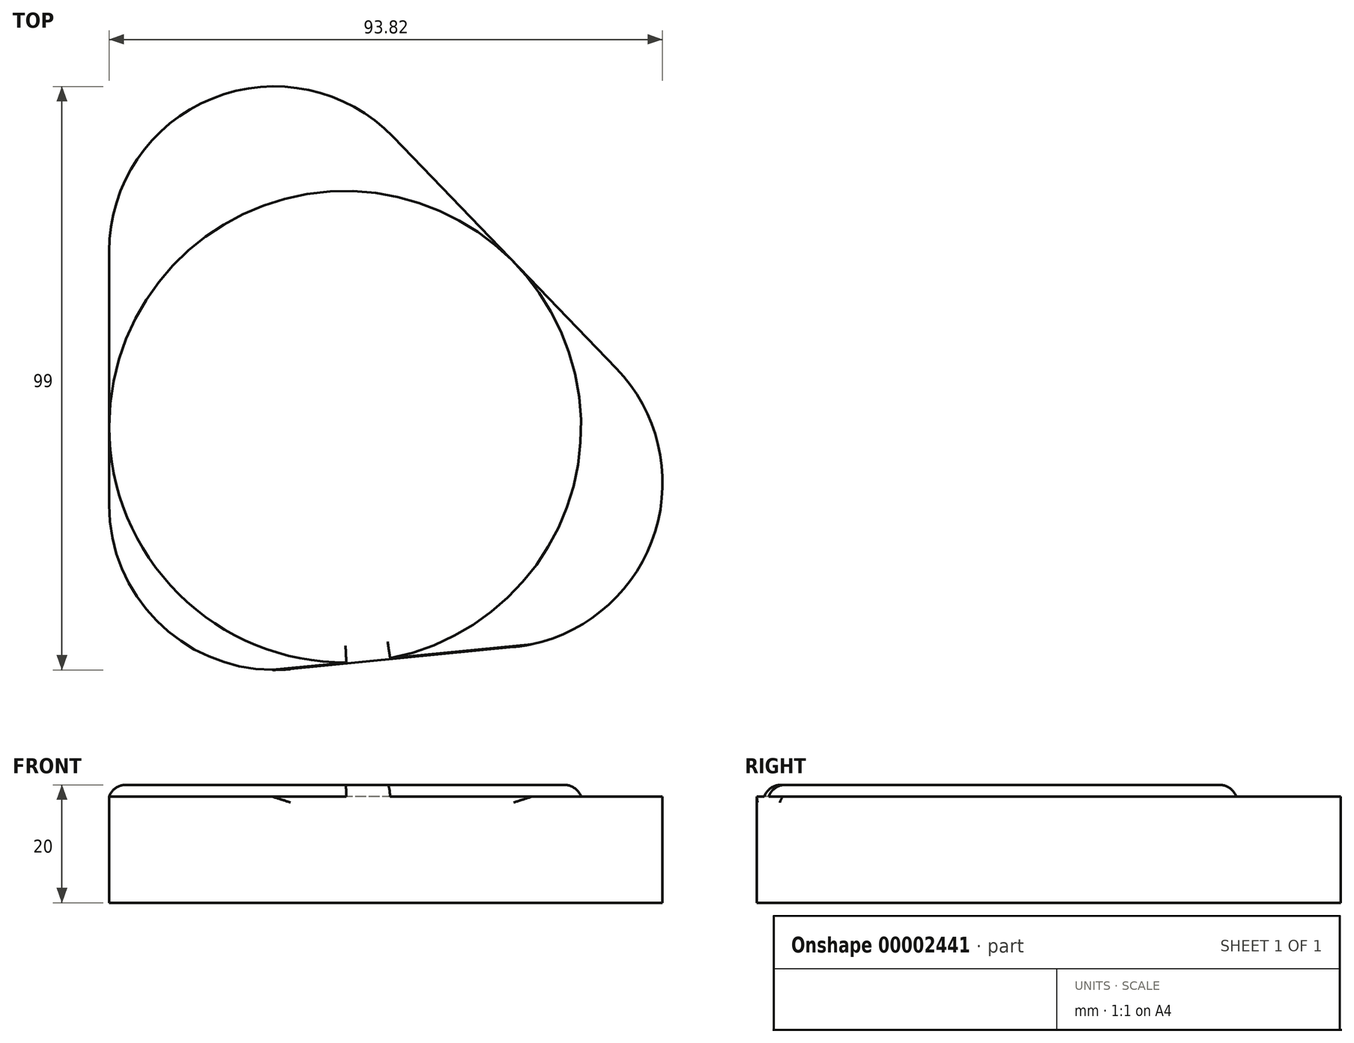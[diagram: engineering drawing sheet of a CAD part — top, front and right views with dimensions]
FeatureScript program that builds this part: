
annotation { "Feature Type Name" : "Feature", "Feature Type Description" : "" }
export const myFeature = defineFeature(function(context is Context, id is Id, definition is map)
    precondition{}
    {
        {
            var Q0;
            Q0=qCreatedBy(makeId("Front.planeOp"),FACE);
            var sketch = newSketch(context, id + "F0", { "sketchPlane" : qUnion([Q0])});
            skArc(sketch, "E0", {"start": v(-40, 18) * mm, "mid": v(-45.93, 9) * mm, "end": v(-40, 0) * mm});
            skLineSegment(sketch, "E1", {"start": v(-40, 0) * mm, "end": v(-40, 18) * mm, "construction": true});
            skLineSegment(sketch, "E2", {"start": v(-40, 18) * mm, "end": v(40, 18) * mm, "construction": true});
            skLineSegment(sketch, "E3", {"start": v(0, 18) * mm, "end": v(0, 0) * mm});
            skLineSegment(sketch, "E4", {"start": v(0, 0) * mm, "end": v(-40, 0) * mm});
            skLineSegment(sketch, "E5", {"start": v(-40, 21) * mm, "end": v(40, 21) * mm, "construction": true});
            skPoint(sketch, "E6", {"position": v(0, 21) * mm});
            skArc(sketch, "E7", {"start": v(40, 18) * mm, "mid": v(20.06, 20.25) * mm, "end": v(0, 21) * mm});
            skLineSegment(sketch, "E8", {"start": v(0, 21) * mm, "end": v(0, 18) * mm});
            skArc(sketch, "E9", {"start": v(0, 21) * mm, "mid": v(-20.06, 20.25) * mm, "end": v(-40, 18) * mm});
            skSolve(sketch);
        }
        {
            var Q0;
            Q0=qCreatedBy(makeId("Top.planeOp"),FACE);
            var sketch = newSketch(context, id + "F1", { "sketchPlane" : qUnion([Q0])});
            skLineSegment(sketch, "E10", {"start": v(8.16, 62.43) * mm, "end": v(45.98, 23.18) * mm});
            skLineSegment(sketch, "E11", {"start": v(28.58, -24.11) * mm, "end": v(-9.24, -27.86) * mm});
            skLineSegment(sketch, "E12", {"start": v(-40, 0) * mm, "end": v(-40, 43) * mm});
            skPoint(sketch, "E13.visualSharp", {"position": v(-40, 112.42) * mm});
            skArc(sketch, "E13.filletArc", {"start": v(8.16, 62.43) * mm, "mid": v(-22.47, 68.97) * mm, "end": v(-40, 43) * mm});
            skPoint(sketch, "E14.visualSharp", {"position": v(86.05, -18.41) * mm});
            skArc(sketch, "E14.filletArc", {"start": v(28.58, -24.11) * mm, "mid": v(52.1, -5.92) * mm, "end": v(45.98, 23.18) * mm});
            skPoint(sketch, "E15.visualSharp", {"position": v(-40, -30.91) * mm});
            skArc(sketch, "E15.filletArc", {"start": v(-40, 0) * mm, "mid": v(-30.8, -20.75) * mm, "end": v(-9.24, -27.86) * mm});
            skCircle(sketch, "E16", {"center": v(0, 13.25) * mm, "radius": 40 * mm});
            skLineSegment(sketch, "E17", {"start": v(0, 13.25) * mm, "end": v(0, 0) * mm, "construction": true});
            skSolve(sketch);
        }
        {
            var Q0;
            Q0=makeQuery(id+"F0.imprint","IMPRINT",FACE,{"disambiguationData":[TD([[makeQuery(id+"F0.imprint","IMPRINT",EDGE,{"derivedFrom":sQuery(id+"F0.wireOp",EDGE,"E0")}),1.0]])]});
            var Q1;
            Q1=sQuery(id+"F0.wireOp",EDGE,"E0");
            var Q2;
            Q2=sQuery(id+"F1.wireOp",EDGE,"E12");
            var Q3;
            Q3=sQuery(id+"F1.wireOp",EDGE,"E13.filletArc");
            var Q4;
            Q4=sQuery(id+"F1.wireOp",EDGE,"E10");
            var Q5;
            Q5=sQuery(id+"F1.wireOp",EDGE,"E14.filletArc");
            var Q6;
            Q6=sQuery(id+"F1.wireOp",EDGE,"E11");
            var Q7;
            Q7=sQuery(id+"F1.wireOp",EDGE,"E15.filletArc");
            sweep(context, id + "F2", {"bodyType" : ToolBodyType.SURFACE, "profiles" : qUnion([Q0]), "surfaceProfiles" : qUnion([Q1]), "path" : qUnion([Q2, Q3, Q4, Q5, Q6, Q7])});
        }
        {
            var Q0;
            {var subQ5=sQuery(id+"F1.wireOp",EDGE,"E15.filletArc");Q0=makeQuery(id+"F1.imprint","IMPRINT",FACE,{"disambiguationData":[TD([[makeQuery(id+"F1.imprint","IMPRINT",EDGE,{"derivedFrom":subQ5}),1.0]])]});}
            var Q1;
            {var subQ5=sQuery(id+"F1.wireOp",EDGE,"E13.filletArc");Q1=makeQuery(id+"F1.imprint","IMPRINT",FACE,{"disambiguationData":[TD([[makeQuery(id+"F1.imprint","IMPRINT",EDGE,{"derivedFrom":subQ5}),1.0]])]});}
            var Q2;
            {var subQ5=sQuery(id+"F1.wireOp",EDGE,"E14.filletArc");Q2=makeQuery(id+"F1.imprint","IMPRINT",FACE,{"disambiguationData":[TD([[makeQuery(id+"F1.imprint","IMPRINT",EDGE,{"derivedFrom":subQ5}),1.0]])]});}
            var Q3;
            Q3=sQuery(id+"F1.wireOp",EDGE,"E12");
            var Q4;
            Q4=sQuery(id+"F1.wireOp",EDGE,"E13.filletArc");
            var Q5;
            Q5=sQuery(id+"F1.wireOp",EDGE,"E10");
            var Q6;
            Q6=sQuery(id+"F1.wireOp",EDGE,"E14.filletArc");
            var Q7;
            Q7=sQuery(id+"F1.wireOp",EDGE,"E11");
            var Q8;
            Q8=sQuery(id+"F1.wireOp",EDGE,"E15.filletArc");
            extrude(context, id + "F3", {"entities" : qUnion([Q0, Q1, Q2]), "surfaceEntities" : qUnion([Q3, Q4, Q5, Q6, Q7, Q8]), "depth" : 18 * mm});
        }
        {
            var Q0;
            {var subQ0=sQuery(id+"F1.wireOp",EDGE,"E16");var subQ2=makeQuery(id+"F1.imprint","INTERSECT",VERTEX,{"derivedFrom":[sQuery(id+"F1.wireOp",EDGE,"E10"),subQ0]});Q0=makeQuery(id+"F1.imprint","IMPRINT",FACE,{"disambiguationData":[TD([[makeQuery(id+"F1.imprint","IMPRINT",EDGE,{"disambiguationData":[TD([[subQ2,-1.0]])],"derivedFrom":subQ0}),1.0]])]});}
            extrude(context, id + "F4", {"entities" : qUnion([Q0]), "operationType" : NewBodyOperationType.ADD, "depth" : 20 * mm});
        }
        {
            var Q0;
            Q0=makeQuery(id+"F4.opExtrude","CAP_FACE",FACE,{"disambiguationData":[OSD([sQuery(id+"F1.wireOp",EDGE,"E16")])],"isStart":false});
            fillet(context, id + "F5", {"entities" : qUnion([Q0]), "radius" : 3 * mm, "tangentPropagation" : true, "allowEdgeOverflow" : false});
        }
    });
